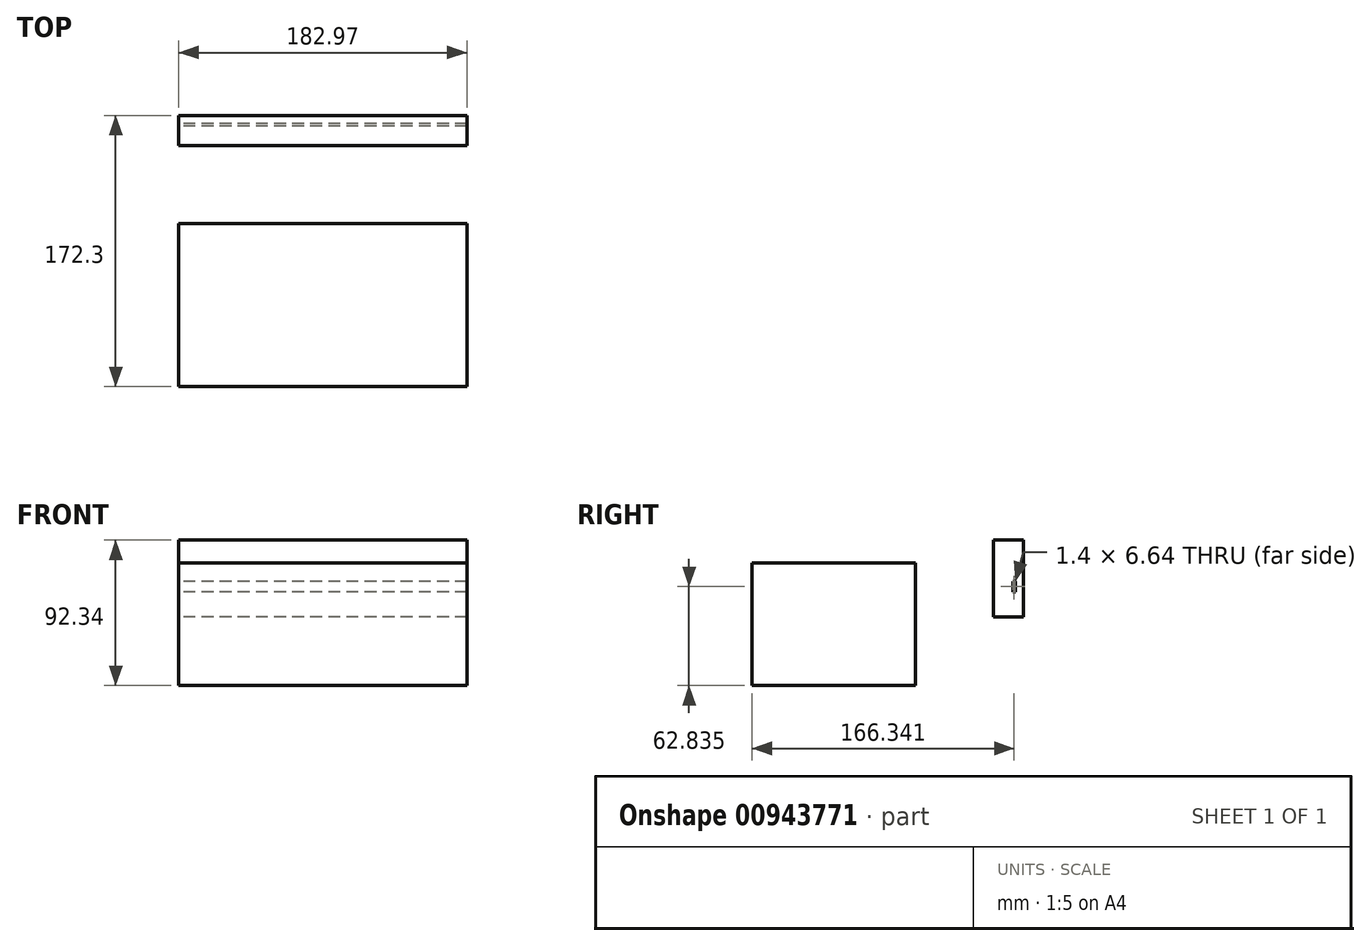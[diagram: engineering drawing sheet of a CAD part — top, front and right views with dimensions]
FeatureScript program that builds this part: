
annotation { "Feature Type Name" : "Feature", "Feature Type Description" : "" }
export const myFeature = defineFeature(function(context is Context, id is Id, definition is map)
    precondition{}
    {
        {
            var Q0;
            Q0=qCreatedBy(makeId("Right.planeOp"),FACE);
            var sketch = newSketch(context, id + "F0", { "sketchPlane" : qUnion([Q0])});
            skLineSegment(sketch, "E0.bottom", {"start": v(-54.34, -16.4) * mm, "end": v(49.34, -16.4) * mm});
            skLineSegment(sketch, "E0.top", {"start": v(-54.34, 61.34) * mm, "end": v(49.34, 61.34) * mm});
            skLineSegment(sketch, "E0.left", {"start": v(-54.34, -16.4) * mm, "end": v(-54.34, 61.34) * mm});
            skLineSegment(sketch, "E0.right", {"start": v(49.34, -16.4) * mm, "end": v(49.34, 61.34) * mm});
            skLineSegment(sketch, "E1.bottom", {"start": v(117.96, 33.23) * mm, "end": v(116.59, 33.23) * mm});
            skLineSegment(sketch, "E1.top", {"start": v(117.96, 27.06) * mm, "end": v(116.59, 27.06) * mm});
            skLineSegment(sketch, "E1.left", {"start": v(117.96, 33.23) * mm, "end": v(117.96, 27.06) * mm});
            skLineSegment(sketch, "E1.right", {"start": v(116.59, 33.23) * mm, "end": v(116.59, 27.06) * mm});
            skLineSegment(sketch, "E2.bottom", {"start": v(98.8, 75.94) * mm, "end": v(117.96, 75.94) * mm});
            skLineSegment(sketch, "E2.top", {"start": v(98.8, 27.06) * mm, "end": v(117.96, 27.06) * mm});
            skLineSegment(sketch, "E2.left", {"start": v(98.8, 75.94) * mm, "end": v(98.8, 27.06) * mm});
            skLineSegment(sketch, "E2.right", {"start": v(117.96, 75.94) * mm, "end": v(117.96, 27.06) * mm});
            skLineSegment(sketch, "E3.bottom", {"start": v(117.96, 65.5) * mm, "end": v(106.7, 65.5) * mm});
            skLineSegment(sketch, "E3.top", {"start": v(117.96, 47.9) * mm, "end": v(106.7, 47.9) * mm});
            skLineSegment(sketch, "E3.left", {"start": v(117.96, 65.5) * mm, "end": v(117.96, 47.9) * mm});
            skLineSegment(sketch, "E3.right", {"start": v(106.7, 65.5) * mm, "end": v(106.7, 47.9) * mm});
            skLineSegment(sketch, "E4.bottom", {"start": v(111.3, 49.75) * mm, "end": v(112.7, 49.75) * mm});
            skLineSegment(sketch, "E4.top", {"start": v(111.3, 43.12) * mm, "end": v(112.7, 43.12) * mm});
            skLineSegment(sketch, "E4.left", {"start": v(111.3, 49.75) * mm, "end": v(111.3, 43.12) * mm});
            skLineSegment(sketch, "E4.right", {"start": v(112.7, 49.75) * mm, "end": v(112.7, 43.12) * mm});
            skSolve(sketch);
        }
        {
            var Q0;
            {var subQ7=sQuery(id+"F0.wireOp",EDGE,"E1.bottom");Q0=makeQuery(id+"F0.imprint","IMPRINT",FACE,{"disambiguationData":[TD([[makeQuery(id+"F0.imprint","IMPRINT",EDGE,{"derivedFrom":subQ7}),-1.0]])]});}
            var Q1;
            {var subQ0=sQuery(id+"F0.wireOp",EDGE,"E1.bottom");Q1=makeQuery(id+"F0.imprint","IMPRINT",FACE,{"disambiguationData":[TD([[makeQuery(id+"F0.imprint","IMPRINT",EDGE,{"derivedFrom":subQ0}),1.0]])]});}
            var Q2;
            Q2=makeQuery(id+"F0.imprint","IMPRINT",FACE,{"disambiguationData":[TD([[makeQuery(id+"F0.imprint","IMPRINT",EDGE,{"derivedFrom":sQuery(id+"F0.wireOp",EDGE,"E3.bottom")}),1.0]])]});
            var Q3;
            Q3=makeQuery(id+"F0.imprint","IMPRINT",FACE,{"disambiguationData":[TD([[makeQuery(id+"F0.imprint","IMPRINT",EDGE,{"derivedFrom":sQuery(id+"F0.wireOp",EDGE,"E0.bottom")}),1.0]])]});
            extrude(context, id + "F1", {"entities" : qUnion([Q0, Q1, Q2, Q3]), "depth" : 182.97 * mm, "offsetDistance" : 25.4 * mm});
        }
    });
